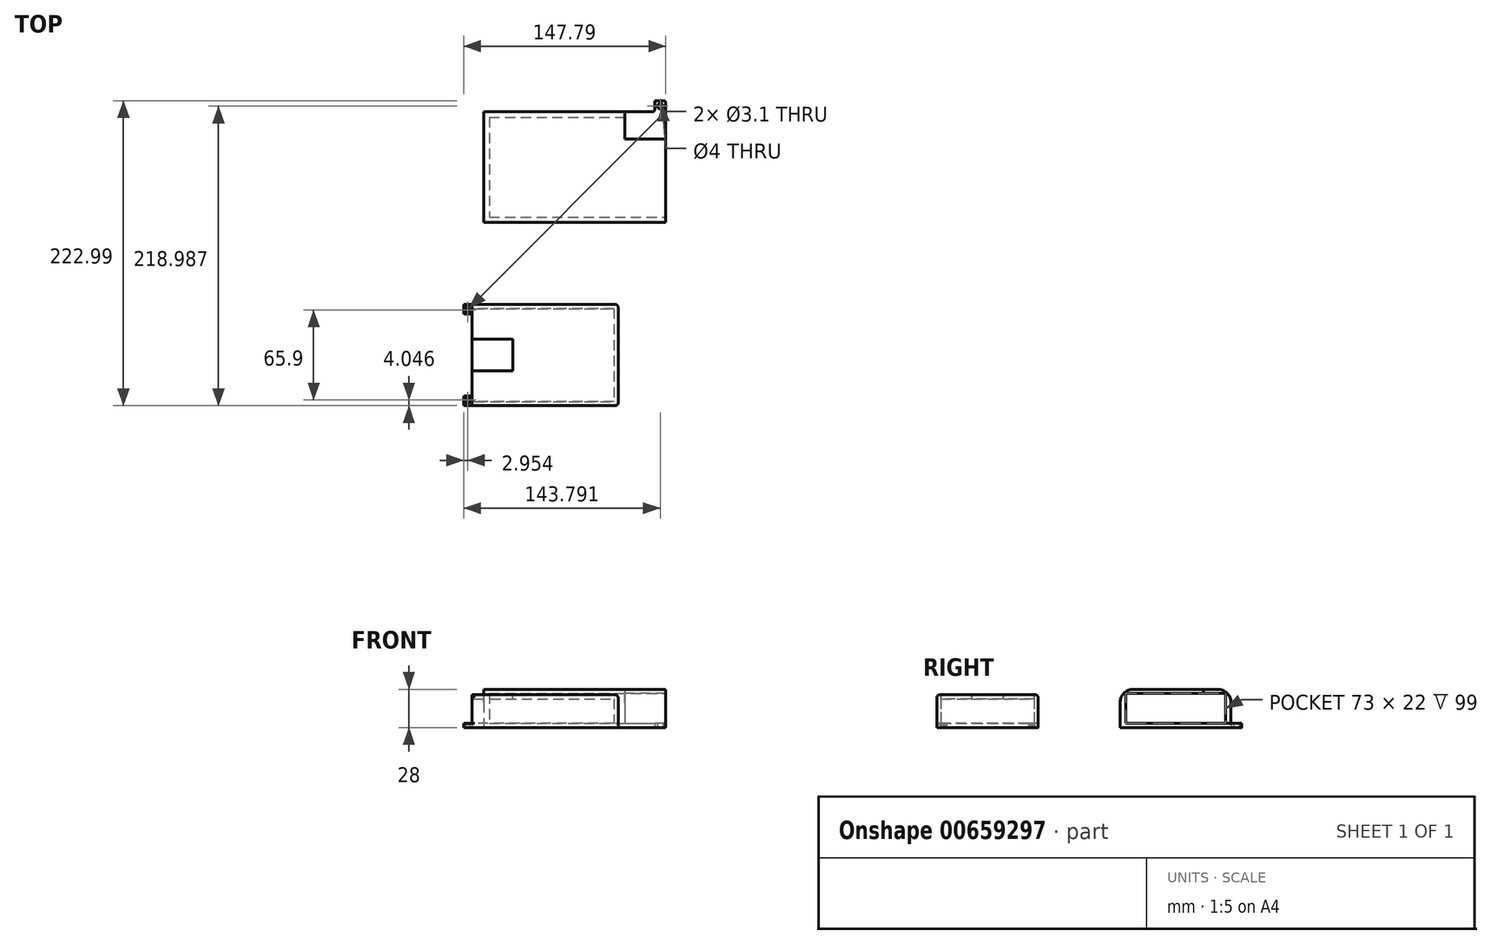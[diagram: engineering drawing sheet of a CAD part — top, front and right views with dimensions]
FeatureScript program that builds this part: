
annotation { "Feature Type Name" : "Feature", "Feature Type Description" : "" }
export const myFeature = defineFeature(function(context is Context, id is Id, definition is map)
    precondition{}
    {
        {
            var Q0;
            Q0=qCreatedBy(makeId("Top.planeOp"),FACE);
            var sketch = newSketch(context, id + "F0", { "sketchPlane" : qUnion([Q0])});
            skLineSegment(sketch, "E0.bottom", {"start": v(-60.08, 63.7) * mm, "end": v(64.92, 63.7) * mm});
            skLineSegment(sketch, "E0.top", {"start": v(-60.08, -9.3) * mm, "end": v(64.92, -9.3) * mm});
            skLineSegment(sketch, "E0.left", {"start": v(-60.08, 63.7) * mm, "end": v(-60.08, -9.3) * mm});
            skLineSegment(sketch, "E0.right", {"start": v(64.92, 63.7) * mm, "end": v(64.92, -9.3) * mm});
            skLineSegment(sketch, "E1.bottom", {"start": v(-64.08, 67.7) * mm, "end": v(68.92, 67.7) * mm});
            skLineSegment(sketch, "E1.top", {"start": v(-64.08, -13.3) * mm, "end": v(68.92, -13.3) * mm});
            skLineSegment(sketch, "E1.left", {"start": v(-64.08, 67.7) * mm, "end": v(-64.08, -13.3) * mm});
            skLineSegment(sketch, "E1.right", {"start": v(68.92, 67.7) * mm, "end": v(68.92, -13.3) * mm});
            skLineSegment(sketch, "E2.bottom", {"start": v(-64.08, 67.7) * mm, "end": v(-56.08, 67.7) * mm});
            skLineSegment(sketch, "E2.top", {"start": v(-64.08, 75.7) * mm, "end": v(-56.08, 75.7) * mm});
            skLineSegment(sketch, "E2.left", {"start": v(-64.08, 67.7) * mm, "end": v(-64.08, 75.7) * mm});
            skLineSegment(sketch, "E2.right", {"start": v(-56.08, 67.7) * mm, "end": v(-56.08, 75.7) * mm});
            skLineSegment(sketch, "E3.bottom", {"start": v(68.92, 67.7) * mm, "end": v(60.92, 67.7) * mm});
            skLineSegment(sketch, "E3.top", {"start": v(68.92, 75.7) * mm, "end": v(60.92, 75.7) * mm});
            skLineSegment(sketch, "E3.left", {"start": v(68.92, 67.7) * mm, "end": v(68.92, 75.7) * mm});
            skLineSegment(sketch, "E3.right", {"start": v(60.92, 67.7) * mm, "end": v(60.92, 75.7) * mm});
            skLineSegment(sketch, "E4.bottom", {"start": v(68.92, -13.3) * mm, "end": v(60.92, -13.3) * mm});
            skLineSegment(sketch, "E4.top", {"start": v(68.92, -21.3) * mm, "end": v(60.92, -21.3) * mm});
            skLineSegment(sketch, "E4.left", {"start": v(68.92, -13.3) * mm, "end": v(68.92, -21.3) * mm});
            skLineSegment(sketch, "E4.right", {"start": v(60.92, -13.3) * mm, "end": v(60.92, -21.3) * mm});
            skLineSegment(sketch, "E5.bottom", {"start": v(-64.08, -13.3) * mm, "end": v(-56.08, -13.3) * mm});
            skLineSegment(sketch, "E5.top", {"start": v(-64.08, -21.3) * mm, "end": v(-56.08, -21.3) * mm});
            skLineSegment(sketch, "E5.left", {"start": v(-64.08, -13.3) * mm, "end": v(-64.08, -21.3) * mm});
            skLineSegment(sketch, "E5.right", {"start": v(-56.08, -13.3) * mm, "end": v(-56.08, -21.3) * mm});
            skCircle(sketch, "E6", {"center": v(-60.08, 71.7) * mm, "radius": 2 * mm});
            skPoint(sketch, "E6.centerSnap0", {"position": v(-60.08, 67.7) * mm});
            skCircle(sketch, "E7", {"center": v(64.92, 71.7) * mm, "radius": 2 * mm});
            skPoint(sketch, "E7.centerSnap0", {"position": v(64.92, 75.7) * mm});
            skCircle(sketch, "E8", {"center": v(64.92, -17.3) * mm, "radius": 2 * mm});
            skPoint(sketch, "E8.centerSnap0", {"position": v(64.92, -21.3) * mm});
            skPoint(sketch, "E8.centerSnap1", {"position": v(68.92, -17.3) * mm});
            skCircle(sketch, "E9", {"center": v(-60.08, -17.3) * mm, "radius": 2 * mm});
            skPoint(sketch, "E9.centerSnap0", {"position": v(-56.08, -17.3) * mm});
            skPoint(sketch, "E9.centerSnap1", {"position": v(-60.08, -21.3) * mm});
            skPoint(sketch, "E10", {"position": v(-56.08, 71.7) * mm});
            skLineSegment(sketch, "E11", {"start": v(64.92, 63.7) * mm, "end": v(68.92, 63.7) * mm});
            skLineSegment(sketch, "E12", {"start": v(64.92, -9.3) * mm, "end": v(68.92, -9.3) * mm});
            skLineSegment(sketch, "E13.bottom", {"start": v(68.92, 67.7) * mm, "end": v(38.92, 67.7) * mm});
            skLineSegment(sketch, "E13.top", {"start": v(68.92, 47.7) * mm, "end": v(38.92, 47.7) * mm});
            skLineSegment(sketch, "E13.left", {"start": v(68.92, 67.7) * mm, "end": v(68.92, 47.7) * mm});
            skLineSegment(sketch, "E13.right", {"start": v(38.92, 67.7) * mm, "end": v(38.92, 47.7) * mm});
            skSolve(sketch);
        }
        {
            var Q0;
            Q0=makeQuery(id+"F0.imprint","IMPRINT",FACE,{"disambiguationData":[TD([[makeQuery(id+"F0.imprint","IMPRINT",EDGE,{"derivedFrom":sQuery(id+"F0.wireOp",EDGE,"E0.top")}),-1.0]])]});
            extrude(context, id + "F1", {"entities" : qUnion([Q0]), "depth" : 25 * mm, "offsetDistance" : 25 * mm});
        }
        {
            var Q0;
            Q0=makeQuery(id+"F0.imprint","IMPRINT",FACE,{"disambiguationData":[TD([[makeQuery(id+"F0.imprint","IMPRINT",EDGE,{"derivedFrom":sQuery(id+"F0.wireOp",EDGE,"E2.bottom")}),1.0]])]});
            var Q1;
            Q1=makeQuery(id+"F0.imprint","IMPRINT",FACE,{"disambiguationData":[TD([[makeQuery(id+"F0.imprint","IMPRINT",EDGE,{"derivedFrom":sQuery(id+"F0.wireOp",EDGE,"E3.top")}),1.0]])]});
            var Q2;
            {var subQ6=sQuery(id+"F0.wireOp",EDGE,"E11");Q2=makeQuery(id+"F0.imprint","IMPRINT",FACE,{"disambiguationData":[TD([[makeQuery(id+"F0.imprint","IMPRINT",EDGE,{"derivedFrom":subQ6}),1.0]])]});}
            var Q3;
            {var subQ3=sQuery(id+"F0.wireOp",EDGE,"E13.right");var subQ5=sQuery(id+"F0.wireOp",EDGE,"E13.top");var subQ7=makeQuery(id+"F0.imprint","INTERSECT",VERTEX,{"derivedFrom":[subQ5,subQ3]});Q3=makeQuery(id+"F0.imprint","IMPRINT",FACE,{"disambiguationData":[TD([[makeQuery(id+"F0.imprint","IMPRINT",EDGE,{"disambiguationData":[TD([[subQ7,1.0]])],"derivedFrom":subQ5}),-1.0]])]});}
            var Q4;
            {var subQ0=sQuery(id+"F0.wireOp",EDGE,"E11");Q4=makeQuery(id+"F0.imprint","IMPRINT",FACE,{"disambiguationData":[TD([[makeQuery(id+"F0.imprint","IMPRINT",EDGE,{"derivedFrom":subQ0}),-1.0]])]});}
            var Q5;
            {var subQ0=sQuery(id+"F0.wireOp",EDGE,"E12");Q5=makeQuery(id+"F0.imprint","IMPRINT",FACE,{"disambiguationData":[TD([[makeQuery(id+"F0.imprint","IMPRINT",EDGE,{"derivedFrom":subQ0}),1.0]])]});}
            var Q6;
            {var subQ1=sQuery(id+"F0.wireOp",EDGE,"E0.top");Q6=makeQuery(id+"F0.imprint","IMPRINT",FACE,{"disambiguationData":[TD([[makeQuery(id+"F0.imprint","IMPRINT",EDGE,{"derivedFrom":subQ1}),1.0]])]});}
            var Q7;
            Q7=makeQuery(id+"F0.imprint","IMPRINT",FACE,{"disambiguationData":[TD([[makeQuery(id+"F0.imprint","IMPRINT",EDGE,{"derivedFrom":sQuery(id+"F0.wireOp",EDGE,"E4.bottom")}),1.0]])]});
            var Q8;
            Q8=makeQuery(id+"F0.imprint","IMPRINT",FACE,{"disambiguationData":[TD([[makeQuery(id+"F0.imprint","IMPRINT",EDGE,{"derivedFrom":sQuery(id+"F0.wireOp",EDGE,"E5.bottom")}),-1.0]])]});
            extrude(context, id + "F2", {"entities" : qUnion([Q0, Q1, Q2, Q3, Q4, Q5, Q6, Q7, Q8]), "operationType" : NewBodyOperationType.ADD, "depth" : 3 * mm, "offsetDistance" : 25 * mm});
        }
        {
            var Q0;
            Q0=makeQuery(id+"F0.imprint","IMPRINT",FACE,{"disambiguationData":[TD([[makeQuery(id+"F0.imprint","IMPRINT",EDGE,{"derivedFrom":sQuery(id+"F0.wireOp",EDGE,"E0.top")}),-1.0]])]});
            var Q1;
            {var subQ1=sQuery(id+"F0.wireOp",EDGE,"E0.top");Q1=makeQuery(id+"F0.imprint","IMPRINT",FACE,{"disambiguationData":[TD([[makeQuery(id+"F0.imprint","IMPRINT",EDGE,{"derivedFrom":subQ1}),1.0]])]});}
            var Q2;
            {var subQ0=sQuery(id+"F0.wireOp",EDGE,"E12");Q2=makeQuery(id+"F0.imprint","IMPRINT",FACE,{"disambiguationData":[TD([[makeQuery(id+"F0.imprint","IMPRINT",EDGE,{"derivedFrom":subQ0}),1.0]])]});}
            extrude(context, id + "F3", {"entities" : qUnion([Q0, Q1, Q2]), "operationType" : NewBodyOperationType.ADD, "depth" : 28 * mm, "offsetDistance" : 25 * mm, "hasSecondDirection" : true, "secondDirectionOppositeDirection" : true, "secondDirectionDepth" : -25 * mm});
        }
        {
            var Q0;
            Q0=makeQuery(id+"F2.opExtrude","CAP_EDGE",EDGE,{"disambiguationData":[OSD([sQuery(id+"F0.wireOp",EDGE,"E4.bottom")])],"isStart":false});
            var Q1;
            Q1=makeQuery(id+"F2.opExtrude","CAP_EDGE",EDGE,{"disambiguationData":[OSD([sQuery(id+"F0.wireOp",EDGE,"E5.bottom")])],"isStart":false});
            var Q2;
            Q2=makeQuery(id+"F2.opExtrude","CAP_EDGE",EDGE,{"disambiguationData":[OSD([sQuery(id+"F0.wireOp",EDGE,"E2.bottom")])],"isStart":false});
            var Q3;
            Q3=makeQuery(id+"F2.opExtrude","CAP_EDGE",EDGE,{"disambiguationData":[OSD([sQuery(id+"F0.wireOp",EDGE,"E3.bottom")])],"isStart":false});
            var Q4;
            Q4=makeQuery(id+"F2.opExtrude","SWEPT_EDGE",EDGE,{"disambiguationData":[OSD([sQuery(id+"F0.wireOp",EDGE,"E1.bottom"),sQuery(id+"F0.wireOp",EDGE,"E3.bottom"),sQuery(id+"F0.wireOp",EDGE,"E3.right")])]});
            var Q5;
            Q5=makeQuery(id+"F2.opExtrude","SWEPT_EDGE",EDGE,{"disambiguationData":[OSD([sQuery(id+"F0.wireOp",EDGE,"E1.bottom"),sQuery(id+"F0.wireOp",EDGE,"E2.bottom"),sQuery(id+"F0.wireOp",EDGE,"E2.right")])]});
            var Q6;
            Q6=makeQuery(id+"F2.opExtrude","SWEPT_EDGE",EDGE,{"disambiguationData":[OSD([sQuery(id+"F0.wireOp",EDGE,"E1.top"),sQuery(id+"F0.wireOp",EDGE,"E5.bottom"),sQuery(id+"F0.wireOp",EDGE,"E5.right")])]});
            var Q7;
            Q7=makeQuery(id+"F2.opExtrude","SWEPT_EDGE",EDGE,{"disambiguationData":[OSD([sQuery(id+"F0.wireOp",EDGE,"E1.top"),sQuery(id+"F0.wireOp",EDGE,"E4.bottom"),sQuery(id+"F0.wireOp",EDGE,"E4.right")])]});
            var Q8;
            Q8=makeQuery(id+"F2.opExtrude","CAP_EDGE",EDGE,{"disambiguationData":[OSD([sQuery(id+"F0.wireOp",EDGE,"E13.right")])],"isStart":false});
            var Q9;
            Q9=makeQuery(id+"F2.opExtrude","SWEPT_EDGE",EDGE,{"disambiguationData":[OSD([sQuery(id+"F0.wireOp",EDGE,"E2.top"),sQuery(id+"F0.wireOp",EDGE,"E2.right")])]});
            var Q10;
            Q10=makeQuery(id+"F2.opExtrude","SWEPT_EDGE",EDGE,{"disambiguationData":[OSD([sQuery(id+"F0.wireOp",EDGE,"E5.top"),sQuery(id+"F0.wireOp",EDGE,"E5.right")])]});
            var Q11;
            Q11=makeQuery(id+"F2.opExtrude","SWEPT_EDGE",EDGE,{"disambiguationData":[OSD([sQuery(id+"F0.wireOp",EDGE,"E5.top"),sQuery(id+"F0.wireOp",EDGE,"E5.left")])]});
            var Q12;
            Q12=makeQuery(id+"F2.opExtrude","SWEPT_EDGE",EDGE,{"disambiguationData":[OSD([sQuery(id+"F0.wireOp",EDGE,"E4.top"),sQuery(id+"F0.wireOp",EDGE,"E4.right")])]});
            var Q13;
            Q13=makeQuery(id+"F2.opExtrude","SWEPT_EDGE",EDGE,{"disambiguationData":[OSD([sQuery(id+"F0.wireOp",EDGE,"E4.top"),sQuery(id+"F0.wireOp",EDGE,"E4.left")])]});
            var Q14;
            Q14=makeQuery(id+"F2.opExtrude","SWEPT_EDGE",EDGE,{"disambiguationData":[OSD([sQuery(id+"F0.wireOp",EDGE,"E3.top"),sQuery(id+"F0.wireOp",EDGE,"E3.left")])]});
            fillet(context, id + "F4", {"entities" : qUnion([Q0, Q1, Q2, Q3, Q4, Q5, Q6, Q7, Q8, Q9, Q10, Q11, Q12, Q13, Q14]), "tangentPropagation" : true, "radius" : 1.5 * mm, "defaultsChanged" : false, "vertexSettings" : [], "allowEdgeOverflow" : false});
        }
        {
            var Q0;
            Q0=makeQuery(id+"F1.opExtrude","CAP_EDGE",EDGE,{"disambiguationData":[OSD([sQuery(id+"F0.wireOp",EDGE,"E0.bottom"),sQuery(id+"F0.wireOp",EDGE,"E11")])],"isStart":false});
            var Q1;
            Q1=makeQuery(id+"F2.opExtrude","CAP_EDGE",EDGE,{"disambiguationData":[OSD([sQuery(id+"F0.wireOp",EDGE,"E0.bottom"),sQuery(id+"F0.wireOp",EDGE,"E11")])],"isStart":false});
            var Q2;
            Q2=makeQuery(id+"F2.opExtrude","CAP_EDGE",EDGE,{"disambiguationData":[OSD([sQuery(id+"F0.wireOp",EDGE,"E0.top"),sQuery(id+"F0.wireOp",EDGE,"E12")])],"isStart":false});
            var Q3;
            Q3=makeQuery(id+"F1.opExtrude","CAP_EDGE",EDGE,{"disambiguationData":[OSD([sQuery(id+"F0.wireOp",EDGE,"E0.top"),sQuery(id+"F0.wireOp",EDGE,"E12")])],"isStart":false});
            var Q4;
            Q4=makeQuery(id+"F3.opExtrude","CAP_EDGE",EDGE,{"disambiguationData":[OSD([sQuery(id+"F0.wireOp",EDGE,"E1.top"),sQuery(id+"F0.wireOp",EDGE,"E4.bottom"),sQuery(id+"F0.wireOp",EDGE,"E5.bottom")])],"isStart":false});
            var Q5;
            Q5=makeQuery(id+"F3.opExtrude","CAP_EDGE",EDGE,{"disambiguationData":[OSD([sQuery(id+"F0.wireOp",EDGE,"E1.bottom"),sQuery(id+"F0.wireOp",EDGE,"E2.bottom")])],"isStart":false});
            fillet(context, id + "F5", {"entities" : qUnion([Q0, Q1, Q2, Q3, Q4, Q5]), "tangentPropagation" : true, "radius" : 9.5 * mm, "defaultsChanged" : false, "vertexSettings" : [], "allowEdgeOverflow" : false});
        }
        {
            var Q0;
            Q0=qCreatedBy(makeId("Top.planeOp"),FACE);
            var sketch = newSketch(context, id + "F6", { "sketchPlane" : qUnion([Q0])});
            skLineSegment(sketch, "E14.bottom", {"start": v(-72.87, -76.3) * mm, "end": v(31.13, -76.3) * mm});
            skLineSegment(sketch, "E14.top", {"start": v(-72.87, -144.3) * mm, "end": v(31.13, -144.3) * mm});
            skLineSegment(sketch, "E14.left", {"start": v(-72.87, -76.3) * mm, "end": v(-72.87, -144.3) * mm});
            skLineSegment(sketch, "E14.right", {"start": v(31.13, -76.3) * mm, "end": v(31.13, -144.3) * mm});
            skLineSegment(sketch, "E15.bottom", {"start": v(-72.87, -147.3) * mm, "end": v(34.13, -147.3) * mm});
            skLineSegment(sketch, "E15.top", {"start": v(-72.87, -73.3) * mm, "end": v(34.13, -73.3) * mm});
            skLineSegment(sketch, "E15.left", {"start": v(-72.87, -147.3) * mm, "end": v(-72.87, -73.3) * mm});
            skLineSegment(sketch, "E15.right", {"start": v(34.13, -147.3) * mm, "end": v(34.13, -73.3) * mm});
            skLineSegment(sketch, "E16.bottom", {"start": v(-72.87, -73.3) * mm, "end": v(-78.87, -73.3) * mm});
            skLineSegment(sketch, "E16.top", {"start": v(-72.87, -80.3) * mm, "end": v(-78.87, -80.3) * mm});
            skLineSegment(sketch, "E16.left", {"start": v(-72.87, -73.3) * mm, "end": v(-72.87, -80.3) * mm});
            skLineSegment(sketch, "E16.right", {"start": v(-78.87, -73.3) * mm, "end": v(-78.87, -80.3) * mm});
            skLineSegment(sketch, "E17.bottom", {"start": v(-72.87, -147.3) * mm, "end": v(-78.87, -147.3) * mm});
            skLineSegment(sketch, "E17.top", {"start": v(-72.87, -140.3) * mm, "end": v(-78.87, -140.3) * mm});
            skLineSegment(sketch, "E17.left", {"start": v(-72.87, -147.3) * mm, "end": v(-72.87, -140.3) * mm});
            skLineSegment(sketch, "E17.right", {"start": v(-78.87, -147.3) * mm, "end": v(-78.87, -140.3) * mm});
            skCircle(sketch, "E18", {"center": v(-75.92, -77.34) * mm, "radius": 1.55 * mm});
            skCircle(sketch, "E19", {"center": v(-75.92, -143.24) * mm, "radius": 1.55 * mm});
            skPoint(sketch, "E19.centerSnap0", {"position": v(-75.87, -80.3) * mm});
            skPoint(sketch, "E20", {"position": v(-72.87, -110.3) * mm});
            skLineSegment(sketch, "E21", {"start": v(-75.92, -110.3) * mm, "end": v(-75.92, -77.34) * mm, "construction": true});
            skLineSegment(sketch, "E22", {"start": v(-75.92, -110.3) * mm, "end": v(-75.92, -143.24) * mm, "construction": true});
            skSolve(sketch);
        }
        {
            var Q0;
            {var subQ0=sQuery(id+"F6.wireOp",EDGE,"E14.bottom");Q0=makeQuery(id+"F6.imprint","IMPRINT",FACE,{"disambiguationData":[TD([[makeQuery(id+"F6.imprint","IMPRINT",EDGE,{"derivedFrom":subQ0}),-1.0]])]});}
            var Q1;
            {var subQ2=sQuery(id+"F6.wireOp",EDGE,"E14.bottom");Q1=makeQuery(id+"F6.imprint","IMPRINT",FACE,{"disambiguationData":[TD([[makeQuery(id+"F6.imprint","IMPRINT",EDGE,{"derivedFrom":subQ2}),1.0]])]});}
            var Q2;
            {var subQ3=sQuery(id+"F6.wireOp",EDGE,"E16.bottom");Q2=makeQuery(id+"F6.imprint","IMPRINT",FACE,{"disambiguationData":[TD([[makeQuery(id+"F6.imprint","IMPRINT",EDGE,{"derivedFrom":subQ3}),1.0]])]});}
            var Q3;
            {var subQ3=sQuery(id+"F6.wireOp",EDGE,"E17.bottom");Q3=makeQuery(id+"F6.imprint","IMPRINT",FACE,{"disambiguationData":[TD([[makeQuery(id+"F6.imprint","IMPRINT",EDGE,{"derivedFrom":subQ3}),-1.0]])]});}
            extrude(context, id + "F7", {"entities" : qUnion([Q0, Q1, Q2, Q3]), "depth" : 3 * mm, "offsetDistance" : 25 * mm});
        }
        {
            var Q0;
            {var subQ2=sQuery(id+"F6.wireOp",EDGE,"E14.bottom");Q0=makeQuery(id+"F6.imprint","IMPRINT",FACE,{"disambiguationData":[TD([[makeQuery(id+"F6.imprint","IMPRINT",EDGE,{"derivedFrom":subQ2}),1.0]])]});}
            extrude(context, id + "F8", {"entities" : qUnion([Q0]), "operationType" : NewBodyOperationType.ADD, "depth" : 21 * mm, "offsetDistance" : 25 * mm});
        }
        {
            var Q0;
            {var subQ2=sQuery(id+"F6.wireOp",EDGE,"E14.bottom");Q0=makeQuery(id+"F6.imprint","IMPRINT",FACE,{"disambiguationData":[TD([[makeQuery(id+"F6.imprint","IMPRINT",EDGE,{"derivedFrom":subQ2}),1.0]])]});}
            var Q1;
            {var subQ0=sQuery(id+"F6.wireOp",EDGE,"E14.bottom");Q1=makeQuery(id+"F6.imprint","IMPRINT",FACE,{"disambiguationData":[TD([[makeQuery(id+"F6.imprint","IMPRINT",EDGE,{"derivedFrom":subQ0}),-1.0]])]});}
            extrude(context, id + "F9", {"entities" : qUnion([Q0, Q1]), "operationType" : NewBodyOperationType.ADD, "depth" : 24 * mm, "offsetDistance" : 25 * mm, "hasSecondDirection" : true, "secondDirectionOppositeDirection" : true, "secondDirectionDepth" : -21 * mm});
        }
        {
            var Q0;
            Q0=makeQuery(id+"F9.opExtrude","CAP_FACE",FACE,{"disambiguationData":[OSD([sQuery(id+"F6.wireOp",EDGE,"E15.bottom"),sQuery(id+"F6.wireOp",EDGE,"E15.top"),sQuery(id+"F6.wireOp",EDGE,"E15.left"),sQuery(id+"F6.wireOp",EDGE,"E15.right")])],"isStart":false});
            var sketch = newSketch(context, id + "F10", { "sketchPlane" : qUnion([Q0])});
            skLineSegment(sketch, "E23.bottom", {"start": v(-72.87, -121.8) * mm, "end": v(-42.87, -121.8) * mm});
            skLineSegment(sketch, "E23.top", {"start": v(-72.87, -98.8) * mm, "end": v(-42.87, -98.8) * mm});
            skLineSegment(sketch, "E23.left", {"start": v(-72.87, -121.8) * mm, "end": v(-72.87, -98.8) * mm});
            skLineSegment(sketch, "E23.right", {"start": v(-42.87, -121.8) * mm, "end": v(-42.87, -98.8) * mm});
            skPoint(sketch, "E24", {"position": v(-72.87, -110.3) * mm});
            skSolve(sketch);
        }
        {
            var Q0;
            Q0=makeQuery(id+"F10.imprint","IMPRINT",FACE,{"disambiguationData":[TD([[makeQuery(id+"F10.imprint","IMPRINT",EDGE,{"derivedFrom":sQuery(id+"F10.wireOp",EDGE,"E23.bottom")}),1.0]])]});
            extrude(context, id + "F11", {"entities" : qUnion([Q0]), "operationType" : NewBodyOperationType.REMOVE, "oppositeDirection" : true, "depth" : 3 * mm, "offsetDistance" : 25 * mm});
        }
        {
            var Q0;
            Q0=makeQuery(id+"F9.opExtrude","CAP_EDGE",EDGE,{"disambiguationData":[OSD([sQuery(id+"F6.wireOp",EDGE,"E15.top")])],"isStart":false});
            var Q1;
            Q1=makeQuery(id+"F9.opExtrude","CAP_EDGE",EDGE,{"disambiguationData":[OSD([sQuery(id+"F6.wireOp",EDGE,"E15.bottom")])],"isStart":false});
            var Q2;
            Q2=makeQuery(id+"F9.opExtrude","CAP_EDGE",EDGE,{"disambiguationData":[OSD([sQuery(id+"F6.wireOp",EDGE,"E15.right")])],"isStart":false});
            var Q3;
            {var subQ0=sQuery(id+"F6.wireOp",EDGE,"E15.right");var subQ1=sQuery(id+"F6.wireOp",EDGE,"E15.bottom");Q3=makeQuery(id+"F9.boolean.opBoolean","MERGE",EDGE,{"derivedFrom":[makeQuery(id+"F8.boolean.opBoolean","MERGE",EDGE,{"derivedFrom":[makeQuery(id+"F7.opExtrude","SWEPT_EDGE",EDGE,{"disambiguationData":[OSD([subQ1,subQ0])]}),makeQuery(id+"F8.opExtrude","SWEPT_EDGE",EDGE,{"disambiguationData":[OSD([subQ1,subQ0])]})]}),makeQuery(id+"F9.opExtrude","SWEPT_EDGE",EDGE,{"disambiguationData":[OSD([subQ1,subQ0])]})]});}
            var Q4;
            {var subQ0=sQuery(id+"F6.wireOp",EDGE,"E15.right");var subQ1=sQuery(id+"F6.wireOp",EDGE,"E15.top");Q4=makeQuery(id+"F9.boolean.opBoolean","MERGE",EDGE,{"derivedFrom":[makeQuery(id+"F8.boolean.opBoolean","MERGE",EDGE,{"derivedFrom":[makeQuery(id+"F7.opExtrude","SWEPT_EDGE",EDGE,{"disambiguationData":[OSD([subQ1,subQ0])]}),makeQuery(id+"F8.opExtrude","SWEPT_EDGE",EDGE,{"disambiguationData":[OSD([subQ1,subQ0])]})]}),makeQuery(id+"F9.opExtrude","SWEPT_EDGE",EDGE,{"disambiguationData":[OSD([subQ1,subQ0])]})]});}
            var Q5;
            {var subQ0=sQuery(id+"F6.wireOp",EDGE,"E17.left");var subQ1=sQuery(id+"F6.wireOp",EDGE,"E17.bottom");var subQ2=sQuery(id+"F6.wireOp",EDGE,"E15.bottom");Q5=makeQuery(id+"F9.boolean.opBoolean","MERGE",EDGE,{"derivedFrom":[makeQuery(id+"F8.opExtrude","SWEPT_EDGE",EDGE,{"disambiguationData":[OSD([subQ2,subQ1,subQ0])]}),makeQuery(id+"F9.opExtrude","SWEPT_EDGE",EDGE,{"disambiguationData":[OSD([subQ2,subQ1,subQ0])]})]});}
            var Q6;
            {var subQ0=sQuery(id+"F6.wireOp",EDGE,"E16.left");var subQ1=sQuery(id+"F6.wireOp",EDGE,"E16.bottom");var subQ2=sQuery(id+"F6.wireOp",EDGE,"E15.top");Q6=makeQuery(id+"F9.boolean.opBoolean","MERGE",EDGE,{"derivedFrom":[makeQuery(id+"F8.opExtrude","SWEPT_EDGE",EDGE,{"disambiguationData":[OSD([subQ2,subQ1,subQ0])]}),makeQuery(id+"F9.opExtrude","SWEPT_EDGE",EDGE,{"disambiguationData":[OSD([subQ2,subQ1,subQ0])]})]});}
            var Q7;
            {var subQ0=sQuery(id+"F6.wireOp",EDGE,"E17.left");var subQ1=sQuery(id+"F6.wireOp",EDGE,"E16.left");var subQ2=sQuery(id+"F6.wireOp",EDGE,"E15.left");Q7=makeQuery(id+"F11.boolean.opBoolean","SPLIT",EDGE,{"disambiguationData":[TD([makeQuery(id+"F8.opExtrude","SWEPT_FACE",FACE,{"disambiguationData":[OSD([sQuery(id+"F6.wireOp",EDGE,"E14.top")])]})])],"derivedFrom":makeQuery(id+"F9.opExtrude","CAP_EDGE",EDGE,{"disambiguationData":[OSD([subQ2,subQ1,subQ0])],"isStart":true})});}
            var Q8;
            {var subQ0=sQuery(id+"F6.wireOp",EDGE,"E17.left");var subQ1=sQuery(id+"F6.wireOp",EDGE,"E16.left");var subQ2=sQuery(id+"F6.wireOp",EDGE,"E15.left");Q8=makeQuery(id+"F11.boolean.opBoolean","SPLIT",EDGE,{"disambiguationData":[TD([makeQuery(id+"F8.opExtrude","SWEPT_FACE",FACE,{"disambiguationData":[OSD([sQuery(id+"F6.wireOp",EDGE,"E14.bottom")])]})])],"derivedFrom":makeQuery(id+"F9.opExtrude","CAP_EDGE",EDGE,{"disambiguationData":[OSD([subQ2,subQ1,subQ0])],"isStart":true})});}
            var Q9;
            Q9=makeQuery(id+"F11.boolean.opBoolean","COPY",EDGE,{"derivedFrom":makeQuery(id+"F11.opExtrude","CAP_EDGE",EDGE,{"disambiguationData":[OSD([sQuery(id+"F10.wireOp",EDGE,"E23.top")])],"isStart":false})});
            var Q10;
            Q10=makeQuery(id+"F11.boolean.opBoolean","COPY",EDGE,{"derivedFrom":makeQuery(id+"F11.opExtrude","CAP_EDGE",EDGE,{"disambiguationData":[OSD([sQuery(id+"F10.wireOp",EDGE,"E23.bottom")])],"isStart":false})});
            var Q11;
            Q11=makeQuery(id+"F11.boolean.opBoolean","COPY",EDGE,{"derivedFrom":makeQuery(id+"F11.opExtrude","CAP_EDGE",EDGE,{"disambiguationData":[OSD([sQuery(id+"F10.wireOp",EDGE,"E23.right")])],"isStart":false})});
            var Q12;
            Q12=makeQuery(id+"F7.opExtrude","CAP_EDGE",EDGE,{"disambiguationData":[OSD([sQuery(id+"F6.wireOp",EDGE,"E15.left")])],"isStart":false});
            fillet(context, id + "F12", {"entities" : qUnion([Q0, Q1, Q2, Q3, Q4, Q5, Q6, Q7, Q8, Q9, Q10, Q11, Q12]), "tangentPropagation" : true, "radius" : 2 * mm, "defaultsChanged" : false, "vertexSettings" : [], "allowEdgeOverflow" : false});
        }
        {
            var Q0;
            Q0=makeQuery(id+"F7.opExtrude","CAP_EDGE",EDGE,{"disambiguationData":[OSD([sQuery(id+"F6.wireOp",EDGE,"E18")])],"isStart":false});
            var Q1;
            Q1=makeQuery(id+"F7.opExtrude","CAP_EDGE",EDGE,{"disambiguationData":[OSD([sQuery(id+"F6.wireOp",EDGE,"E19")])],"isStart":false});
            chamfer(context, id + "F13", {"entities" : qUnion([Q0, Q1]), "width" : 1 * mm, "tangentPropagation" : true});
        }
    });
